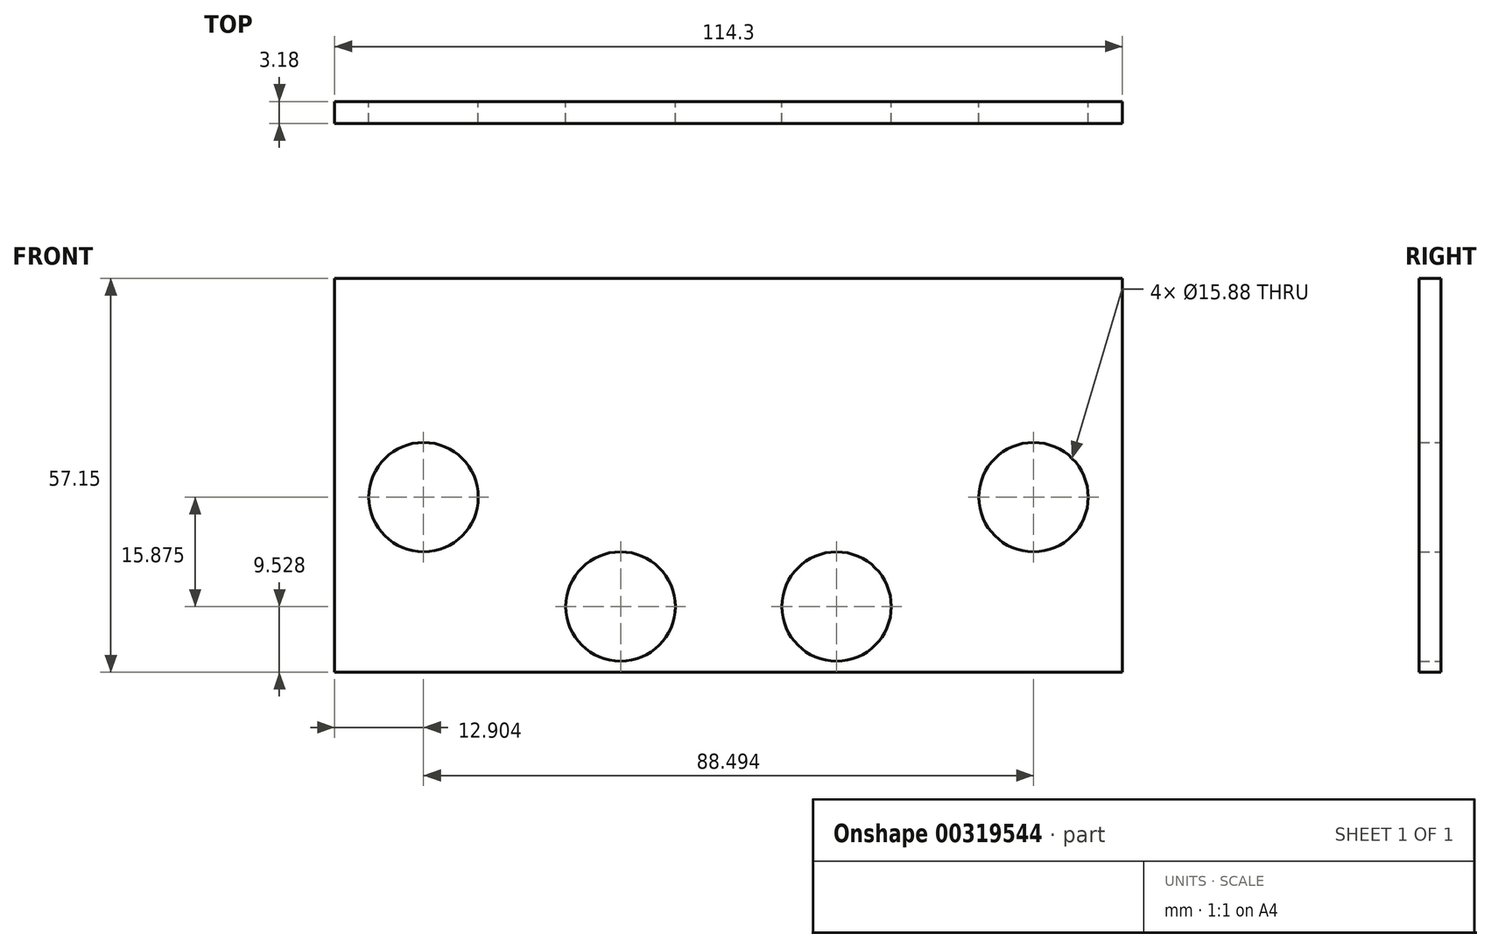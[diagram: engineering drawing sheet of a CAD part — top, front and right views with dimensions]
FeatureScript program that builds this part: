
annotation { "Feature Type Name" : "Feature", "Feature Type Description" : "" }
export const myFeature = defineFeature(function(context is Context, id is Id, definition is map)
    precondition{}
    {
        {
            var Q0;
            Q0=qCreatedBy(makeId("Front.planeOp"),FACE);
            var sketch = newSketch(context, id + "F0", { "sketchPlane" : qUnion([Q0])});
            skCircle(sketch, "E0", {"center": v(-63.02, -15.39) * mm, "radius": 7.94 * mm});
            skCircle(sketch, "E1", {"center": v(-34.44, -31.26) * mm, "radius": 7.94 * mm});
            skCircle(sketch, "E2", {"center": v(-3.1, -31.26) * mm, "radius": 7.94 * mm});
            skCircle(sketch, "E3", {"center": v(25.48, -15.39) * mm, "radius": 7.94 * mm});
            skLineSegment(sketch, "E4.bottom", {"start": v(-75.92, -40.79) * mm, "end": v(38.38, -40.79) * mm});
            skLineSegment(sketch, "E4.top", {"start": v(-75.92, 16.36) * mm, "end": v(38.38, 16.36) * mm});
            skLineSegment(sketch, "E4.left", {"start": v(-75.92, -40.79) * mm, "end": v(-75.92, 16.36) * mm});
            skLineSegment(sketch, "E4.right", {"start": v(38.38, -40.79) * mm, "end": v(38.38, 16.36) * mm});
            skLineSegment(sketch, "E5.bottom", {"start": v(-50.52, 16.36) * mm, "end": v(-28.3, 16.36) * mm});
            skLineSegment(sketch, "E5.top", {"start": v(-50.52, 0.49) * mm, "end": v(-28.3, 0.49) * mm});
            skLineSegment(sketch, "E5.left", {"start": v(-50.52, 16.36) * mm, "end": v(-50.52, 0.49) * mm});
            skLineSegment(sketch, "E5.right", {"start": v(-28.3, 16.36) * mm, "end": v(-28.3, 0.49) * mm});
            skLineSegment(sketch, "E6.top", {"start": v(-9.24, 0.49) * mm, "end": v(12.98, 0.49) * mm});
            skLineSegment(sketch, "E6.left", {"start": v(-9.24, 16.36) * mm, "end": v(-9.24, 0.49) * mm});
            skLineSegment(sketch, "E6.right", {"start": v(12.98, 16.36) * mm, "end": v(12.98, 0.49) * mm});
            skSolve(sketch);
        }
        {
            var Q0;
            Q0 = qSketchRegion(id + "F0", true);
            extrude(context, id + "F1", {"entities" : qUnion([Q0]), "depth" : 3.17 * mm});
        }
    });
